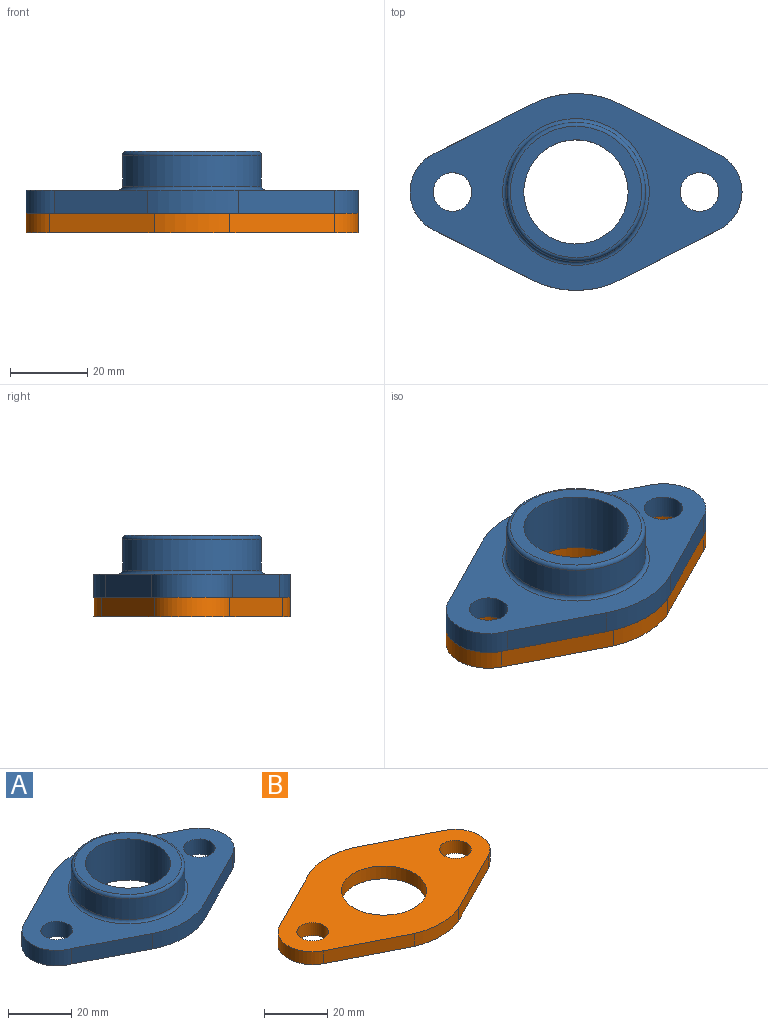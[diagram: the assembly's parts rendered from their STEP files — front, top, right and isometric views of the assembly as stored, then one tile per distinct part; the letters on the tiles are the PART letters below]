
ASSEMBLY  parts=2 mates=1
PART A: 17 faces, bbox 86x51x16 mm
  f0: plane 23.98x12.3mm, normal (-0.46,-0.89,0), area 161.7mm2, adj f1,f9,f10,f11
  f1: cylinder r=25.5mm len=23.63mm, axis (0,0,-1), area 147.4mm2, adj f0,f2,f10,f11
  f2: plane 24.99x12.7mm, normal (0.45,-0.89,0), area 168.2mm2, adj f1,f3,f10,f11
  f3: cylinder r=11mm len=19.61mm, axis (0,0,-1), area 145.3mm2, adj f2,f4,f10,f11
  f4: plane 24.99x12.7mm, normal (0.45,0.89,0), area 168.2mm2, adj f3,f5,f10,f11
  f5: cylinder r=25.5mm len=23.98mm, axis (0,0,-1), area 149.8mm2, adj f4,f6,f10,f11
  f6: plane 23.63x12.12mm, normal (-0.46,0.89,0), area 159.3mm2, adj f5,f9,f10,f11
  f7: cylinder r=5mm len=10mm, axis (0,0,-1), area 188.5mm2, adj f10,f11
  f8: cylinder r=5mm len=10mm, axis (0,0,-1), area 188.5mm2, adj f10,f11
  f9: cylinder r=11mm len=20.77mm, axis (0,0,-1), area 163.1mm2, adj f0,f6,f10,f11
  f10: plane 86x51mm, normal (0,0,1), area 1666.2mm2, adj f0,f1,f2,f3,f4,f5,f6,f7
  f11: plane 86x51mm, normal (0,0,-1), area 2227.7mm2, adj f0,f1,f2,f3,f4,f5,f6,f7
  f12: cylinder r=13.5mm len=27mm, axis (0,0,-1), area 1357.2mm2, adj f11,f14
  f13: cylinder r=18mm len=36mm, axis (0,0,-1), area 904.8mm2, adj f15,f16
  f14: plane 34x34mm, normal (0,0,1), area 335.4mm2, adj f12,f16
  f15: torus R=19mm, axis (0,0,1), area 181.2mm2, adj f10,f13
  f16: torus R=17mm, axis (0,0,1), area 174.1mm2, adj f13,f14
PART B: 13 faces, bbox 86x51x5 mm
  f0: plane 27.13x13.71mm, normal (0.45,0.89,0), area 152mm2, adj f1,f8,f11,f12
  f1: cylinder r=25.5mm len=19.67mm, axis (0,0,-1), area 100.9mm2, adj f0,f2,f11,f12
  f2: plane 27.13x13.71mm, normal (-0.45,0.89,0), area 152mm2, adj f1,f3,f11,f12
  f3: cylinder r=11mm len=19.64mm, axis (0,0,-1), area 121.3mm2, adj f2,f4,f11,f12
  f4: plane 27.13x13.71mm, normal (-0.45,-0.89,0), area 152mm2, adj f3,f5,f11,f12
  f5: cylinder r=25.5mm len=19.67mm, axis (0,0,-1), area 100.9mm2, adj f4,f6,f11,f12
  f6: plane 27.13x13.71mm, normal (0.45,-0.89,0), area 152mm2, adj f5,f8,f11,f12
  f7: cylinder r=13.5mm len=27mm, axis (0,0,-1), area 424.1mm2, adj f11,f12
  f8: cylinder r=11mm len=19.64mm, axis (0,0,-1), area 121.3mm2, adj f0,f6,f11,f12
  f9: cylinder r=5mm len=10mm, axis (0,0,-1), area 157.1mm2, adj f11,f12
  f10: cylinder r=5mm len=10mm, axis (0,0,-1), area 157.1mm2, adj f11,f12
  f11: plane 86x51mm, normal (0,0,1), area 2226.6mm2, adj f0,f1,f2,f3,f4,f5,f6,f7
  f12: plane 86x51mm, normal (0,0,-1), area 2226.6mm2, adj f0,f1,f2,f3,f4,f5,f6,f7
PLACE A t=(-8.84,16.06,-28.34)mm
PLACE B t=(-8.84,16.06,-33.34)mm
MATE fastened A.f12 <-> B.f7  axis (0,0,-1) through (-8.84,16.06,-28.34)mm
